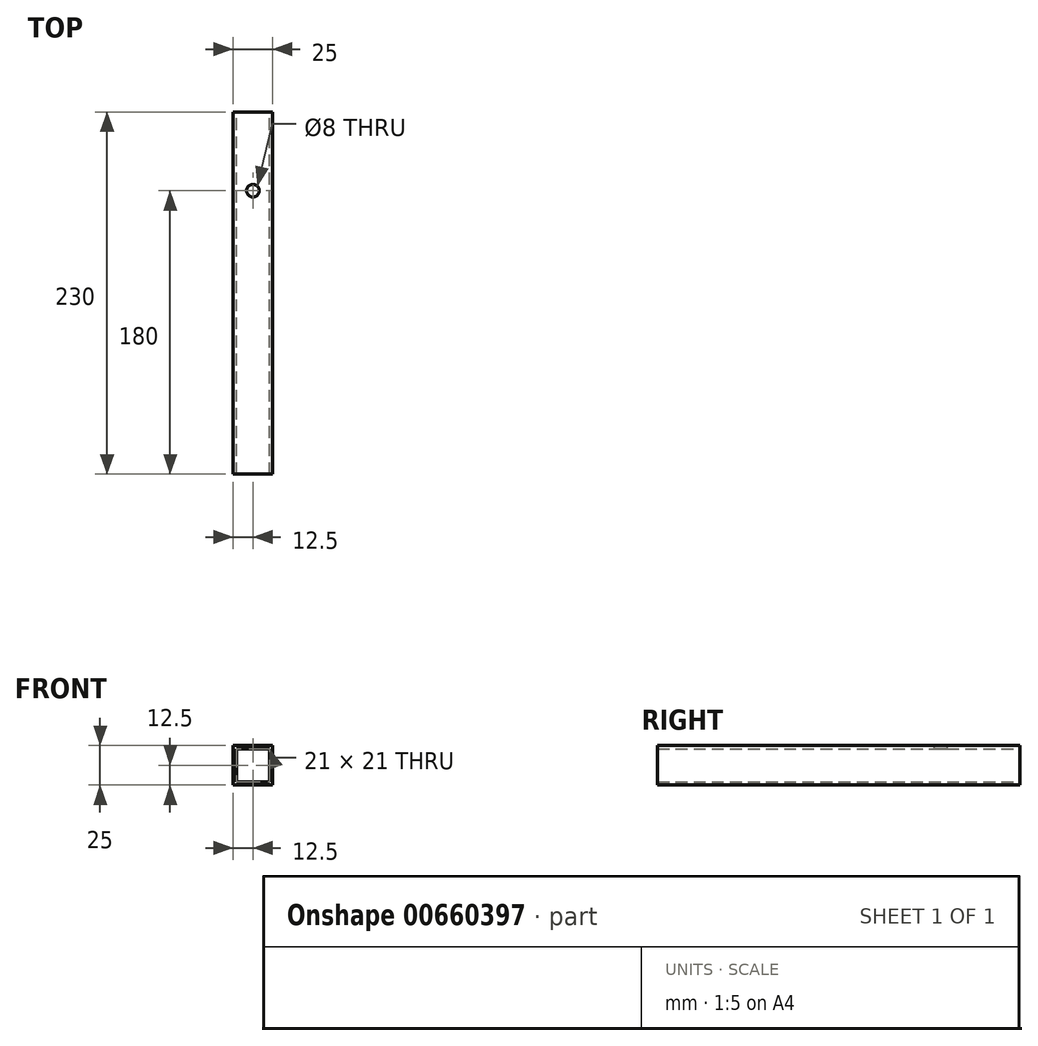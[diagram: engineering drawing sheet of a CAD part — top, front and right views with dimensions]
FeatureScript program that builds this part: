
annotation { "Feature Type Name" : "Feature", "Feature Type Description" : "" }
export const myFeature = defineFeature(function(context is Context, id is Id, definition is map)
    precondition{}
    {
        {
            var Q0;
            Q0=qCreatedBy(makeId("Front.planeOp"),FACE);
            var sketch = newSketch(context, id + "F0", { "sketchPlane" : qUnion([Q0])});
            skLineSegment(sketch, "E0.bottom", {"start": v(0, 0) * mm, "end": v(25, 0) * mm});
            skLineSegment(sketch, "E0.top", {"start": v(0, 25) * mm, "end": v(25, 25) * mm});
            skLineSegment(sketch, "E0.left", {"start": v(0, 0) * mm, "end": v(0, 25) * mm});
            skLineSegment(sketch, "E0.right", {"start": v(25, 0) * mm, "end": v(25, 25) * mm});
            skLineSegment(sketch, "E1.0", {"start": v(2, 23) * mm, "end": v(23, 23) * mm});
            skLineSegment(sketch, "E1.1", {"start": v(2, 2) * mm, "end": v(2, 23) * mm});
            skLineSegment(sketch, "E1.2", {"start": v(2, 2) * mm, "end": v(23, 2) * mm});
            skLineSegment(sketch, "E1.3", {"start": v(23, 2) * mm, "end": v(23, 23) * mm});
            skSolve(sketch);
        }
        {
            var Q0;
            Q0=makeQuery(id+"F0.imprint","IMPRINT",FACE,{"disambiguationData":[TD([[makeQuery(id+"F0.imprint","IMPRINT",EDGE,{"derivedFrom":sQuery(id+"F0.wireOp",EDGE,"E0.bottom")}),1.0]])]});
            extrude(context, id + "F1", {"entities" : qUnion([Q0]), "depth" : 230 * mm, "offsetDistance" : 25 * mm});
        }
        {
            var Q0;
            Q0=makeQuery(id+"F1.opExtrude","SWEPT_FACE",FACE,{"disambiguationData":[OSD([sQuery(id+"F0.wireOp",EDGE,"E0.top")])]});
            var sketch = newSketch(context, id + "F2", { "sketchPlane" : qUnion([Q0])});
            skPoint(sketch, "E2", {"position": v(12.5, -50) * mm});
            skSolve(sketch);
        }
        {
            var Q0;
            Q0=sQuery(id+"F2.wireOp",VERTEX,"E2");
            var Q1;
            Q1=makeQuery(id+"F1.opExtrude","SWEPT_BODY",BODY,{"disambiguationData":[OSD([sQuery(id+"F0.wireOp",EDGE,"E0.bottom"),sQuery(id+"F0.wireOp",EDGE,"E0.top"),sQuery(id+"F0.wireOp",EDGE,"E0.left"),sQuery(id+"F0.wireOp",EDGE,"E0.right"),sQuery(id+"F0.wireOp",EDGE,"E1.0"),sQuery(id+"F0.wireOp",EDGE,"E1.1"),sQuery(id+"F0.wireOp",EDGE,"E1.2"),sQuery(id+"F0.wireOp",EDGE,"E1.3")])]});
            hole(context, id + "F3", {"style" : HoleStyle.SIMPLE, "endStyle" : HoleEndStyle.BLIND, "holeDiameter" : 8 * mm, "majorDiameter" : 5 * mm, "holeDepth" : 5 * mm, "isTappedThrough" : true, "tappedDepth" : 12 * mm, "tapClearance" : 3, "startFromSketch" : true, "locations" : qUnion([Q0]), "scope" : qUnion([Q1])});
        }
    });
